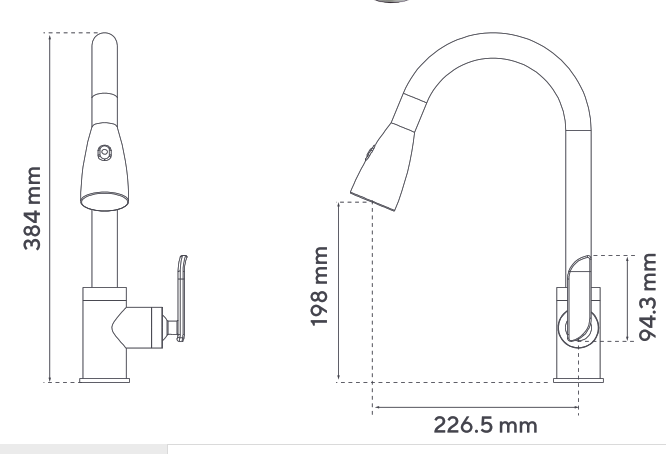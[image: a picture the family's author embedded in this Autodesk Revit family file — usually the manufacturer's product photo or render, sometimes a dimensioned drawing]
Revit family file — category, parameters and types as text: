
# Revit family: 01-3808-11 MONOMANDO LAVAPLATOS MAIRA
name_source: partatom
category: Aparatos sanitarios
revit_build: Autodesk Revit 2018 (Build: 20170223_1515(x64)
units: mm (PartAtom-declared; Revit-internal decimal feet)

## family parameters
Anfitrión = Cara
Compartido = No
Corte con vacíos al cargar = No
Cota de conector redondo = Diámetro de uso
Número OmniClass = 23.31.11.00
Punto de cálculo de habitación = No
Tipo de pieza = Normal

## types (1)
- 01-0903-11
    Alto = 384 mm
    Alto - aireador = 198 mm  [stored 0.649606 ft]
    Ancho - aireador = 226.5 mm
    Conexión AC = Sí
    Conexión AF = Sí
    Conexión de residuos = No
    Conexión de ventilación = No
    Descripción = Bimando
    Elevación por defecto = 0 mm  [stored 0 ft]
    Fabricante = Gricol
    Imagen de tipo = MEZCLADOR LAVAMANOS PLÁSTICO 8”-4” HELVETIA.jpg
    Link Ficha Tecnica = http://infotecnica.gricol.com
    Metal Laton Cromado = Metal Laton Cromado
    Metal Zamak Cromado = Metal Zamak Cromado
    Modelo = 01-0903-11
    Product Name = MEZCLADOR LAVAMANOS PLÁSTICO 8”-4” HELVETIA
    URL = https://www.gricol.com

note: [stored X ft] marks values corroborated as IEEE doubles in the binary element streams (Revit-internal decimal feet)

## geometry (parser evidence)
native form markers: Blend x2, Sweep x3
no freeform markers — native parametric forms only
